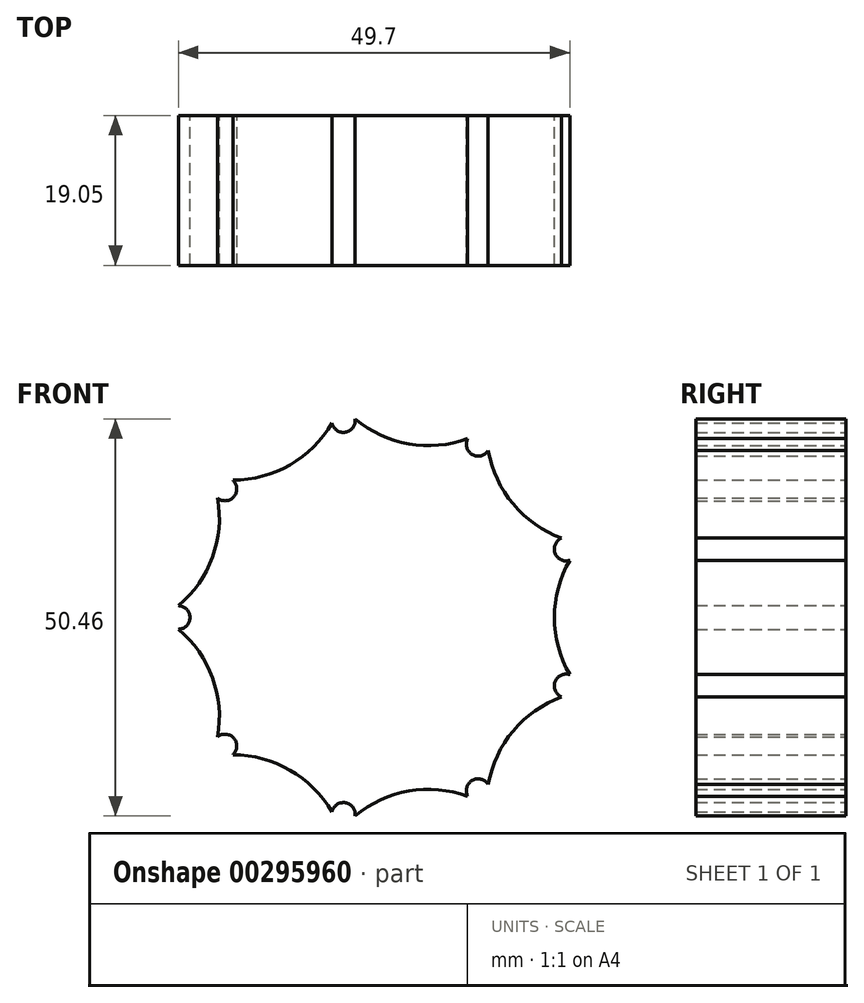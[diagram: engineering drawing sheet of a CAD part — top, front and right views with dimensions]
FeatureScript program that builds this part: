
annotation { "Feature Type Name" : "Feature", "Feature Type Description" : "" }
export const myFeature = defineFeature(function(context is Context, id is Id, definition is map)
    precondition{}
    {
        {
            var Q0;
            Q0=qCreatedBy(makeId("Front.planeOp"),FACE);
            var sketch = newSketch(context, id + "F0", { "sketchPlane" : qUnion([Q0])});
            skCircle(sketch, "E0", {"center": v(0, 0) * mm, "radius": 25.4 * mm});
            skCircle(sketch, "E1", {"center": v(-25.4, 0) * mm, "radius": 1.5 * mm});
            skLineSegment(sketch, "E2", {"start": v(-25.4, 0) * mm, "end": v(0, 0) * mm, "construction": true});
            skLineSegment(sketch, "E3", {"start": v(0, 0) * mm, "end": v(-19.46, -16.33) * mm, "construction": true});
            skCircle(sketch, "E4", {"center": v(-19.46, -16.33) * mm, "radius": 1.5 * mm});
            skArc(sketch, "E5", {"start": v(-20.39, -15.15) * mm, "mid": v(-21.05, -7.66) * mm, "end": v(-25.36, -1.5) * mm});
            skArc(sketch, "E6.1.1", {"start": v(-5.88, -24.71) * mm, "mid": v(-11.2, -19.4) * mm, "end": v(-18.46, -17.45) * mm});
            skCircle(sketch, "E6.2.0", {"center": v(-4.41, -25.01) * mm, "radius": 1.5 * mm});
            skArc(sketch, "E6.2.1", {"start": v(11.38, -22.7) * mm, "mid": v(3.89, -22.06) * mm, "end": v(-2.93, -25.23) * mm});
            skCircle(sketch, "E6.3.0", {"center": v(12.7, -22) * mm, "radius": 1.5 * mm});
            skArc(sketch, "E6.3.1", {"start": v(23.31, -10.08) * mm, "mid": v(17.16, -14.4) * mm, "end": v(13.98, -21.2) * mm});
            skCircle(sketch, "E6.4.0", {"center": v(23.87, -8.69) * mm, "radius": 1.5 * mm});
            skArc(sketch, "E6.4.1", {"start": v(24.34, 7.26) * mm, "mid": v(22.4, 0) * mm, "end": v(24.34, -7.26) * mm});
            skCircle(sketch, "E6.5.0", {"center": v(23.87, 8.69) * mm, "radius": 1.5 * mm});
            skArc(sketch, "E6.5.1", {"start": v(13.98, 21.2) * mm, "mid": v(17.16, 14.4) * mm, "end": v(23.31, 10.08) * mm});
            skCircle(sketch, "E6.6.0", {"center": v(12.7, 22) * mm, "radius": 1.5 * mm});
            skArc(sketch, "E6.6.1", {"start": v(-2.93, 25.23) * mm, "mid": v(3.89, 22.06) * mm, "end": v(11.38, 22.7) * mm});
            skCircle(sketch, "E6.7.0", {"center": v(-4.41, 25.01) * mm, "radius": 1.5 * mm});
            skArc(sketch, "E6.7.1", {"start": v(-18.46, 17.45) * mm, "mid": v(-11.2, 19.4) * mm, "end": v(-5.88, 24.71) * mm});
            skCircle(sketch, "E6.8.0", {"center": v(-19.46, 16.33) * mm, "radius": 1.5 * mm});
            skArc(sketch, "E6.8.1", {"start": v(-25.36, 1.5) * mm, "mid": v(-21.05, 7.66) * mm, "end": v(-20.39, 15.15) * mm});
            skSolve(sketch);
        }
        {
            var Q0;
            {var subQ7=sQuery(id+"F0.wireOp",EDGE,"E5");Q0=makeQuery(id+"F0.imprint","IMPRINT",FACE,{"disambiguationData":[TD([[makeQuery(id+"F0.imprint","IMPRINT",EDGE,{"derivedFrom":subQ7}),-1.0]])]});}
            extrude(context, id + "F1", {"entities" : qUnion([Q0]), "depth" : 19.05 * mm});
        }
    });
